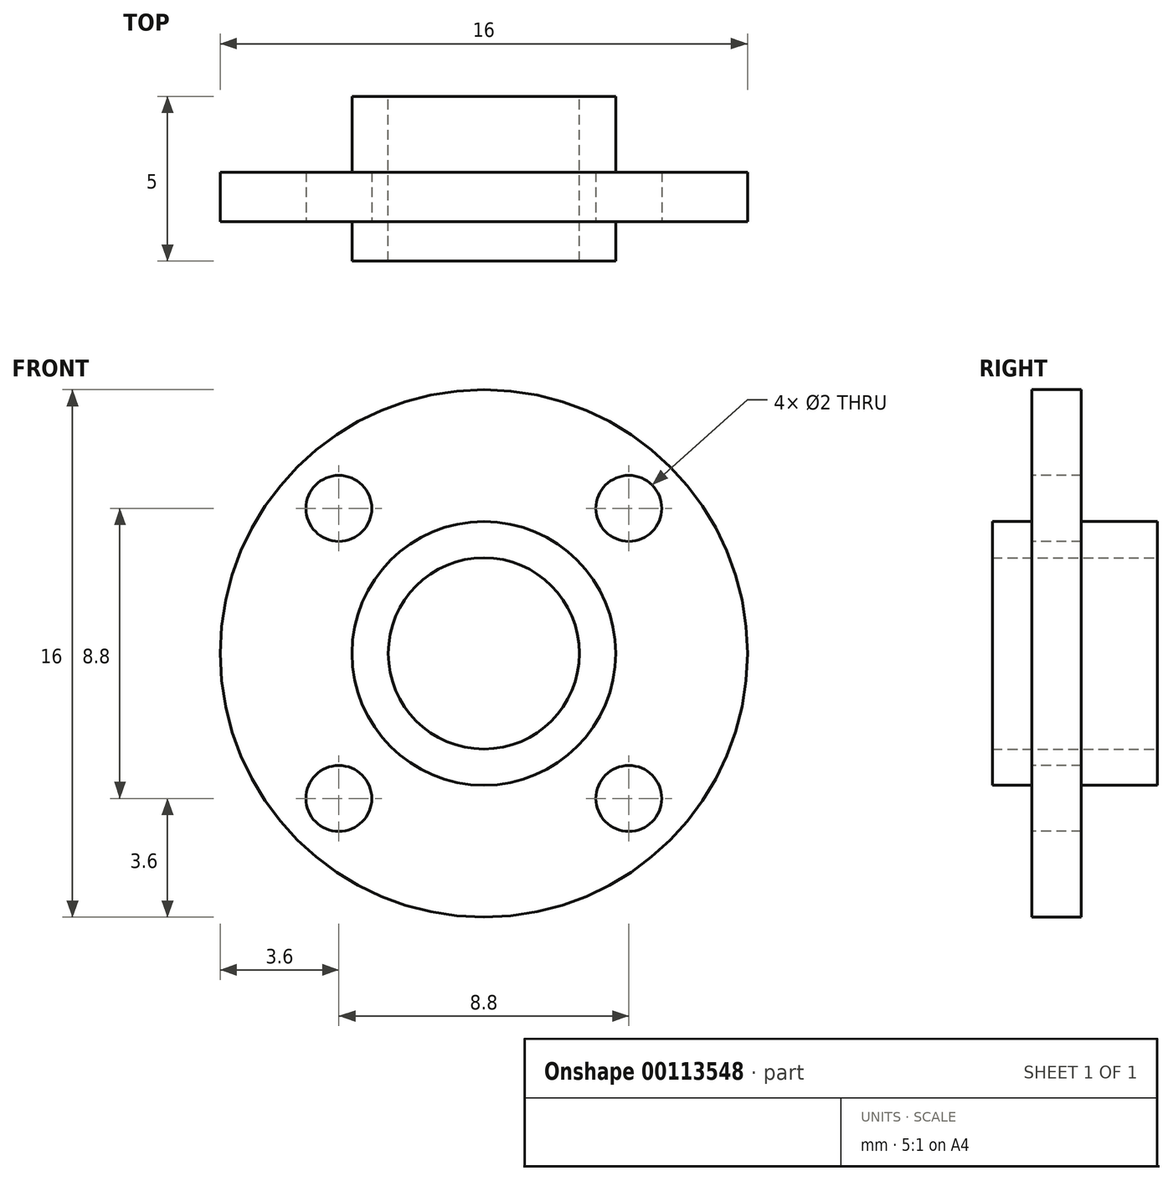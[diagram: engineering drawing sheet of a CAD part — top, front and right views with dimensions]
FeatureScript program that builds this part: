
annotation { "Feature Type Name" : "Feature", "Feature Type Description" : "" }
export const myFeature = defineFeature(function(context is Context, id is Id, definition is map)
    precondition{}
    {
        {
            var Q0;
            Q0=qCreatedBy(makeId("Front.planeOp"),FACE);
            var sketch = newSketch(context, id + "F0", { "sketchPlane" : qUnion([Q0])});
            skCircle(sketch, "E0", {"center": v(0, 0) * mm, "radius": 8 * mm});
            skSolve(sketch);
        }
        {
            var Q0;
            Q0=qSketchRegion(id+"F0",true);
            extrude(context, id + "F1", {"entities" : qUnion([Q0]), "depth" : 1.5 * mm});
        }
        {
            var Q0;
            Q0=makeQuery(id+"F1.opExtrude","CAP_FACE",FACE,{"disambiguationData":[OSD([sQuery(id+"F0.wireOp",EDGE,"E0")])],"isStart":false});
            var sketch = newSketch(context, id + "F2", { "sketchPlane" : qUnion([Q0])});
            skCircle(sketch, "E1", {"center": v(4.4, 4.4) * mm, "radius": 1 * mm});
            skLineSegment(sketch, "E2", {"start": v(0, 8) * mm, "end": v(0, -8) * mm, "construction": true});
            skLineSegment(sketch, "E3", {"start": v(-8, 0) * mm, "end": v(8, 0) * mm, "construction": true});
            skCircle(sketch, "E4.MirrorC", {"center": v(-4.4, 4.4) * mm, "radius": 1 * mm});
            skCircle(sketch, "E5.MirrorC", {"center": v(-4.4, -4.4) * mm, "radius": 1 * mm});
            skCircle(sketch, "E6.MirrorC", {"center": v(4.4, -4.4) * mm, "radius": 1 * mm});
            skSolve(sketch);
        }
        {
            var Q0;
            Q0=sQuery(id+"F2.wireOp",VERTEX,"E4.MirrorC.center");
            var Q1;
            Q1=sQuery(id+"F2.wireOp",VERTEX,"E1.center");
            var Q2;
            Q2=sQuery(id+"F2.wireOp",VERTEX,"E6.MirrorC.center");
            var Q3;
            Q3=sQuery(id+"F2.wireOp",VERTEX,"E5.MirrorC.center");
            var Q4;
            Q4=makeQuery(id+"F1.opExtrude","SWEPT_BODY",BODY,{"disambiguationData":[OSD([sQuery(id+"F0.wireOp",EDGE,"E0")])]});
            hole(context, id + "F3", {"style" : HoleStyle.SIMPLE, "holeDiameter" : 2 * mm, "endStyle" : HoleEndStyle.THROUGH, "locations" : qUnion([Q0, Q1, Q2, Q3]), "scope" : qUnion([Q4])});
        }
        {
            var Q0;
            Q0=makeQuery(id+"F1.opExtrude","CAP_FACE",FACE,{"disambiguationData":[OSD([sQuery(id+"F0.wireOp",EDGE,"E0")])],"isStart":false});
            var sketch = newSketch(context, id + "F4", { "sketchPlane" : qUnion([Q0])});
            skCircle(sketch, "E7", {"center": v(0, 0) * mm, "radius": 4 * mm});
            skSolve(sketch);
        }
        {
            var Q0;
            Q0=qSketchRegion(id+"F4",true);
            extrude(context, id + "F5", {"entities" : qUnion([Q0]), "operationType" : NewBodyOperationType.ADD, "depth" : 1.2 * mm});
        }
        {
            var Q0;
            Q0=makeQuery(id+"F1.opExtrude","CAP_FACE",FACE,{"disambiguationData":[OSD([sQuery(id+"F0.wireOp",EDGE,"E0")])],"isStart":true});
            var sketch = newSketch(context, id + "F6", { "sketchPlane" : qUnion([Q0])});
            skCircle(sketch, "E8", {"center": v(0, 0) * mm, "radius": 4 * mm});
            skSolve(sketch);
        }
        {
            var Q0;
            Q0=qSketchRegion(id+"F6",true);
            extrude(context, id + "F7", {"entities" : qUnion([Q0]), "operationType" : NewBodyOperationType.ADD, "depth" : 2.3 * mm});
        }
        {
            var Q0;
            Q0=makeQuery(id+"F7.opExtrude","CAP_FACE",FACE,{"disambiguationData":[OSD([sQuery(id+"F6.wireOp",EDGE,"E8")])],"isStart":false});
            var sketch = newSketch(context, id + "F8", { "sketchPlane" : qUnion([Q0])});
            skCircle(sketch, "E9", {"center": v(0, 0) * mm, "radius": 2.9 * mm});
            skSolve(sketch);
        }
        {
            var Q0;
            Q0=sQuery(id+"F8.wireOp",VERTEX,"E9.center");
            var Q1;
            Q1=makeQuery(id+"F1.opExtrude","SWEPT_BODY",BODY,{"disambiguationData":[OSD([sQuery(id+"F0.wireOp",EDGE,"E0")])]});
            hole(context, id + "F9", {"style" : HoleStyle.SIMPLE, "holeDiameter" : 5.8 * mm, "endStyle" : HoleEndStyle.THROUGH, "locations" : qUnion([Q0]), "scope" : qUnion([Q1])});
        }
    });
